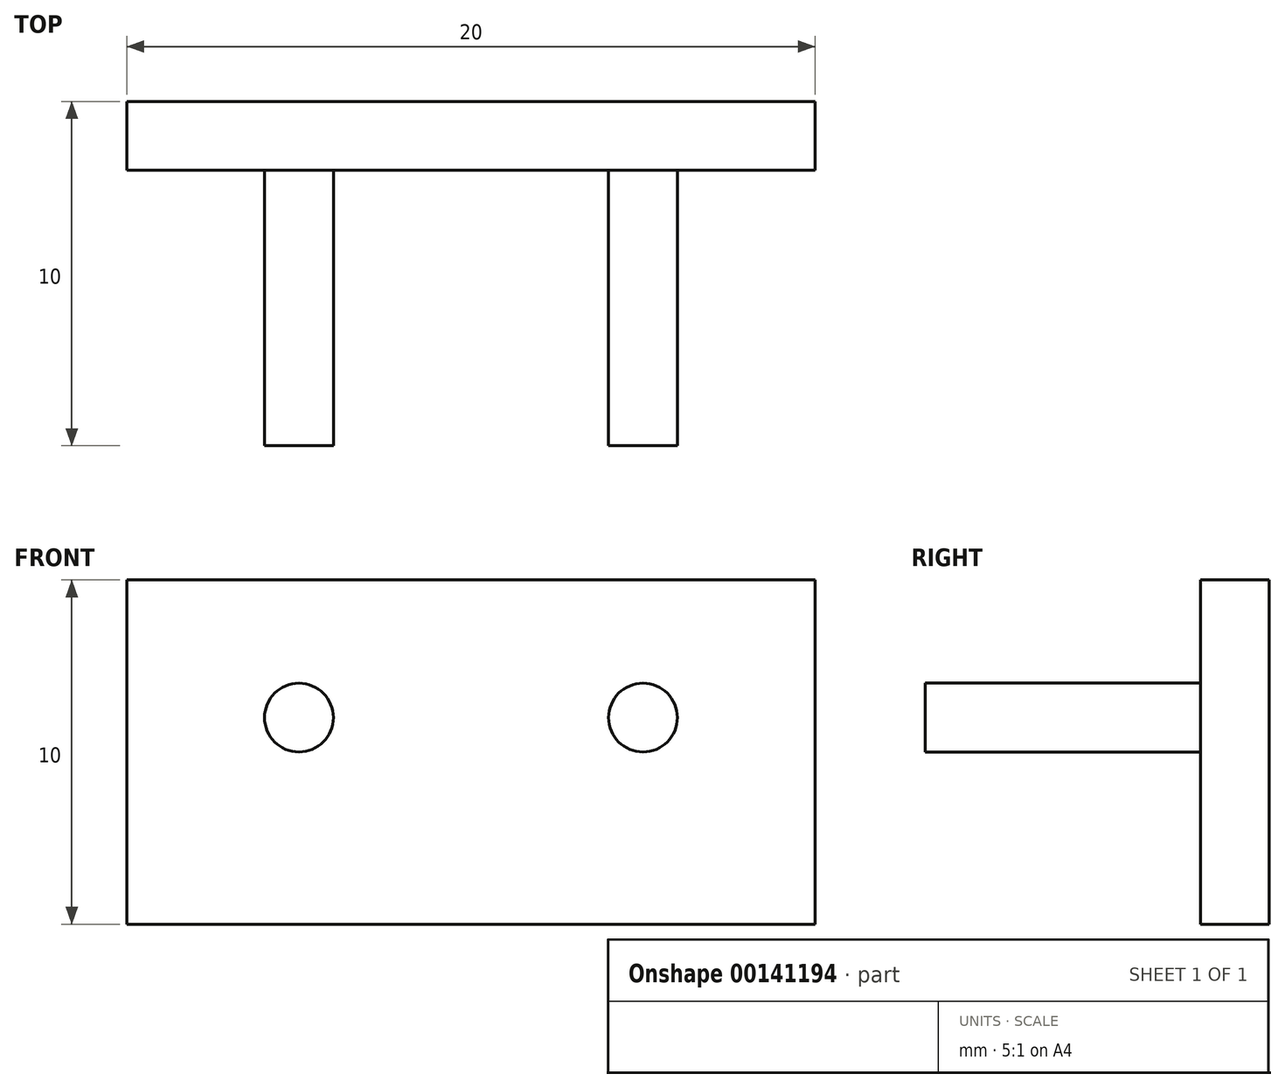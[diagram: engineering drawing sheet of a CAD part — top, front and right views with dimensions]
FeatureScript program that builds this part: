
annotation { "Feature Type Name" : "Feature", "Feature Type Description" : "" }
export const myFeature = defineFeature(function(context is Context, id is Id, definition is map)
    precondition{}
    {
        {
            var Q0;
            Q0=qCreatedBy(makeId("Front.planeOp"),FACE);
            var sketch = newSketch(context, id + "F0", { "sketchPlane" : qUnion([Q0])});
            skLineSegment(sketch, "E0.bottom", {"start": v(-10, 5) * mm, "end": v(10, 5) * mm});
            skLineSegment(sketch, "E0.top", {"start": v(-10, -5) * mm, "end": v(10, -5) * mm});
            skLineSegment(sketch, "E0.left", {"start": v(-10, 5) * mm, "end": v(-10, -5) * mm});
            skLineSegment(sketch, "E0.right", {"start": v(10, 5) * mm, "end": v(10, -5) * mm});
            skSolve(sketch);
        }
        {
            var Q0;
            Q0=makeQuery(id+"F0.imprint","IMPRINT",FACE,{"disambiguationData":[TD([[makeQuery(id+"F0.imprint","IMPRINT",EDGE,{"derivedFrom":sQuery(id+"F0.wireOp",EDGE,"E0.bottom")}),-1.0]])]});
            extrude(context, id + "F1", {"entities" : qUnion([Q0]), "depth" : 2 * mm, "offsetDistance" : 25 * mm});
        }
        {
            var Q0;
            Q0=makeQuery(id+"F1.opExtrude","CAP_FACE",FACE,{"disambiguationData":[OSD([sQuery(id+"F0.wireOp",EDGE,"E0.bottom"),sQuery(id+"F0.wireOp",EDGE,"E0.top"),sQuery(id+"F0.wireOp",EDGE,"E0.left"),sQuery(id+"F0.wireOp",EDGE,"E0.right")])],"isStart":false});
            var sketch = newSketch(context, id + "F2", { "sketchPlane" : qUnion([Q0])});
            skCircle(sketch, "E1", {"center": v(-5, 1) * mm, "radius": 1 * mm});
            skCircle(sketch, "E2", {"center": v(5, 1) * mm, "radius": 1 * mm});
            skSolve(sketch);
        }
        {
            var Q0;
            Q0=makeQuery(id+"F2.imprint","IMPRINT",FACE,{"disambiguationData":[TD([[makeQuery(id+"F2.imprint","IMPRINT",EDGE,{"derivedFrom":sQuery(id+"F2.wireOp",EDGE,"E1")}),1.0]])]});
            var Q1;
            Q1=makeQuery(id+"F2.imprint","IMPRINT",FACE,{"disambiguationData":[TD([[makeQuery(id+"F2.imprint","IMPRINT",EDGE,{"derivedFrom":sQuery(id+"F2.wireOp",EDGE,"E2")}),1.0]])]});
            extrude(context, id + "F3", {"entities" : qUnion([Q0, Q1]), "operationType" : NewBodyOperationType.ADD, "depth" : 8 * mm, "offsetDistance" : 25 * mm});
        }
    });
